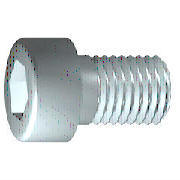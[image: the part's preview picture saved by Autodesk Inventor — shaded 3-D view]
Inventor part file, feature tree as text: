
AUTODESK INVENTOR PART (.ipt)
format: ipt  version: 2020 (Build 240168000, 168)  size: 194,560 bytes
history: native  units: mm (DEFAULTED — no unit token found)
features: sketch x2, other x1, extrude x1, plane x1, fillet x1
ambient origin geometry x7: Origin, YZ Plane, XY Plane, X Axis, Y Axis, Z Axis, Center Point
bodies: Solid1 (feature_tree)
feature tree (6):
  other  "Bryła"
  extrude  "Szczelina"  Depth=10.0mm
  plane  "Work Plane1"
  fillet  "Fillet2"  Radius=0.49086mm
  sketch  "Szkic1"
  sketch  "Szkic2"
